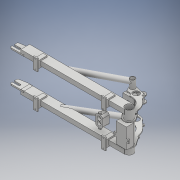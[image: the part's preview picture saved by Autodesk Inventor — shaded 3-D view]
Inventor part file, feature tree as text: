
AUTODESK INVENTOR PART (.ipt)
format: ipt  version: 2019.2 (Build 232265000, 265)  size: 694,272 bytes
history: native  units: mm
features: extrude x18, sketch x18, other x11, fillet x4, plane x3, mirror x2, projected_geometry x1
ambient origin geometry x8: Origin, YZ Plane, XZ Plane, XY Plane, X Axis, Y Axis, Z Axis, Center Point
bodies: Solid1 (feature_tree), Solid2 (feature_tree), Solid3 (feature_tree), Solid7 (feature_tree), Solid12 (feature_tree)
feature tree (57):
  other  "Swingarm.ipt"
  plane  "Work Plane1"
  extrude  "Extrusion1"  [1 undecoded]
  extrude  "Extrusion3"  Depth=44.25mm TaperAngle=0.0deg
  extrude  "Extrusion4"  Depth=4.0mm
  plane  "Work Plane2"
  mirror  "Mirror4"
  mirror  "Mirror5"
  plane  "Work Plane3"
  extrude  "Extrusion5"  [1 undecoded]
  extrude  "Extrusion6"  Depth=27.0mm TaperAngle=0.0deg
  extrude  "Extrusion7"  Depth=54.0mm TaperAngle=0.0deg
  extrude  "Extrusion9"  Depth=65.0mm
  fillet  "Fillet2"  Radius=3.25mm
  extrude  "Extrusion10"  Depth=9.5mm
  extrude  "Extrusion11"  Depth=30.0mm TaperAngle=0.0deg
  extrude  "Extrusion14"  Depth=18.0mm
  extrude  "Extrusion12"  Depth=10.0mm TaperAngle=0.0deg
  extrude  "Extrusion13"  Depth=4.0mm
  fillet  "Fillet3"  Radius=4.0mm
  extrude  "Extrusion15"  Depth=29.0mm
  extrude  "Extrusion16"  Depth=5.0mm TaperAngle=0.0deg
  extrude  "Extrusion17"  Depth=34.0mm TaperAngle=0.0deg
  extrude  "Extrusion18"  Depth=4.0mm
  extrude  "Extrusion20"  Depth=19.25mm TaperAngle=0.0deg
  fillet  "Fillet4"  Radius=19.25mm
  extrude  "Extrusion24"  Depth=26.0mm
  fillet  "Fillet5"  [1 undecoded]
  other  "Arms::Swingarm.ipt"
  other  "FrontMotorPlate::Swingarm.ipt"
  other  "ShockPlate::Swingarm.ipt"
  other  "TaggingFeature1"
  sketch  "Sketch1"  dims[d0=10.0mm d1=-35.0mm]
  other  "JigPartA"
  sketch  "Sketch4"  dims[d2=44.25mm d3=0.0mm d8=44.25mm d9=0.0mm]
  sketch  "Sketch5"  dims[d10=4.0mm d11=4.0mm]
  other  "BackMotorPlate::Swingarm.ipt"
  sketch  "Sketch6"  dims[d12=5.0mm d13=0.0mm d14=-235.5mm]
  other  "JigPartB-up"
  sketch  "Sketch7"  dims[d15=132.0mm d16=27.0mm d17=0.0mm]
  sketch  "Sketch8"  dims[d18=23.0mm d19=0.0mm d20=54.0mm d21=0.0mm]
  sketch  "Sketch10"  dims[d24=29.25mm d25=0.0mm d26=65.0mm d28=3.25mm]
  sketch  "Sketch11"  dims[d29=9.5mm d30=9.5mm]
  sketch  "Sketch12"  dims[d31=29.25mm d32=0.0mm d33=30.0mm d34=0.0mm]
  other  "JigPartB-bottom"
  sketch  "Sketch13"  dims[d35=30.0mm d36=0.0mm d37=18.0mm]
  sketch  "Sketch14"  dims[d38=18.0mm d39=10.0mm d40=0.0mm]
  sketch  "Sketch15"  dims[d41=9.0mm d42=4.0mm d43=4.0mm]
  sketch  "Sketch16"  dims[d44=29.0mm d45=29.0mm]
  sketch  "Sketch17"  dims[d46=5.0mm d47=0.0mm d48=5.0mm d49=0.0mm]
  other  "JigPartC"
  sketch  "Sketch18"  dims[d50=34.0mm d51=0.0mm d52=34.0mm d53=0.0mm]
  sketch  "Sketch19"  dims[d54=4.0mm d55=4.0mm]
  sketch  "Sketch21"  dims[d56=5.0mm d57=0.0mm d60=170.25mm d61=0.0mm d70=19.25mm]
  other  "Dropout::Swingarm.ipt"
  sketch  "Sketch25"  dims[d71=10.0mm d72=0.0mm d73=26.0mm]
  projected_geometry  "Project Cut Edges2"
note: 3 required parameter values undecoded (feature->parameter linkage not recoverable at this tier; creation-order binding heuristic only, values carry confidence <= 0.55)
